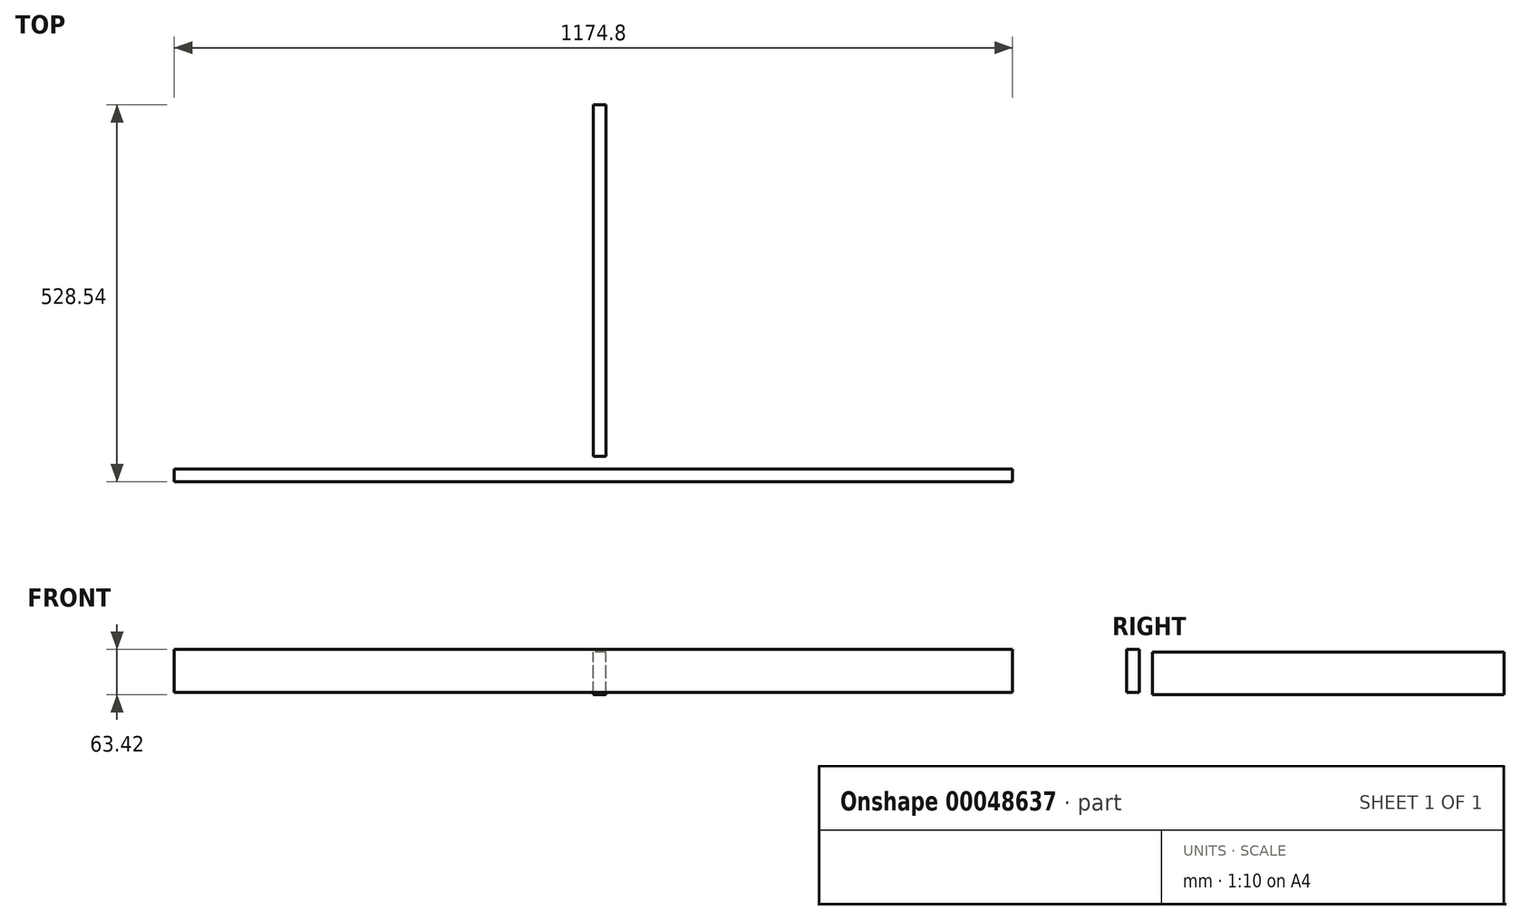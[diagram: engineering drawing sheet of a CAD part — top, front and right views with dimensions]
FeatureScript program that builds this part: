
annotation { "Feature Type Name" : "Feature", "Feature Type Description" : "" }
export const myFeature = defineFeature(function(context is Context, id is Id, definition is map)
    precondition{}
    {
        {
            assignVariable(context, id + "F0", {"name" : "mat1", "anyValue" : 17.6});
        }
        {
            var Q0;
            Q0=qCreatedBy(makeId("Front.planeOp"),FACE);
            var sketch = newSketch(context, id + "F1", { "sketchPlane" : qUnion([Q0])});
            skLineSegment(sketch, "E0.rect.bottom", {"start": v(587.4, 30) * mm, "end": v(-587.4, 30) * mm});
            skLineSegment(sketch, "E0.rect.top", {"start": v(587.4, -30) * mm, "end": v(-587.4, -30) * mm});
            skLineSegment(sketch, "E0.rect.left", {"start": v(587.4, 30) * mm, "end": v(587.4, -30) * mm});
            skLineSegment(sketch, "E0.rect.right", {"start": v(-587.4, 30) * mm, "end": v(-587.4, -30) * mm});
            skPoint(sketch, "E0.rect.middle", {"position": v(0, 0) * mm});
            skSolve(sketch);
        }
        {
            var Q0;
            Q0=makeQuery(id+"F1.imprint","IMPRINT",FACE,{"disambiguationData":[TD([[makeQuery(id+"F1.imprint","IMPRINT",EDGE,{"derivedFrom":sQuery(id+"F1.wireOp",EDGE,"E0.rect.bottom")}),1.0]])]});
            extrude(context, id + "F2", {"entities" : qUnion([Q0]), "depth" : (getVariable(context, 'mat1')) * mm});
        }
        {
            var Q0;
            Q0=qCreatedBy(makeId("Right.planeOp"),FACE);
            var sketch = newSketch(context, id + "F3", { "sketchPlane" : qUnion([Q0])});
            skLineSegment(sketch, "E1.bottom", {"start": v(18.14, -33.42) * mm, "end": v(510.94, -33.42) * mm});
            skLineSegment(sketch, "E1.top", {"start": v(18.14, 26.58) * mm, "end": v(510.94, 26.58) * mm});
            skLineSegment(sketch, "E1.left", {"start": v(18.14, -33.42) * mm, "end": v(18.14, 26.58) * mm});
            skLineSegment(sketch, "E1.right", {"start": v(510.94, -33.42) * mm, "end": v(510.94, 26.58) * mm});
            skSolve(sketch);
        }
        {
            var Q0;
            Q0=makeQuery(id+"F3.imprint","IMPRINT",FACE,{"disambiguationData":[TD([[makeQuery(id+"F3.imprint","IMPRINT",EDGE,{"derivedFrom":sQuery(id+"F3.wireOp",EDGE,"E1.bottom")}),1.0]])]});
            var Q1;
            Q1=sQuery(id+"F3.wireOp",EDGE,"E1.bottom");
            var Q2;
            Q2=sQuery(id+"F3.wireOp",EDGE,"E1.top");
            var Q3;
            Q3=sQuery(id+"F3.wireOp",EDGE,"E1.left");
            var Q4;
            Q4=sQuery(id+"F3.wireOp",EDGE,"E1.right");
            extrude(context, id + "F4", {"entities" : qUnion([Q0]), "surfaceEntities" : qUnion([Q1, Q2, Q3, Q4]), "depth" : (getVariable(context, 'mat1')) * mm});
        }
    });
